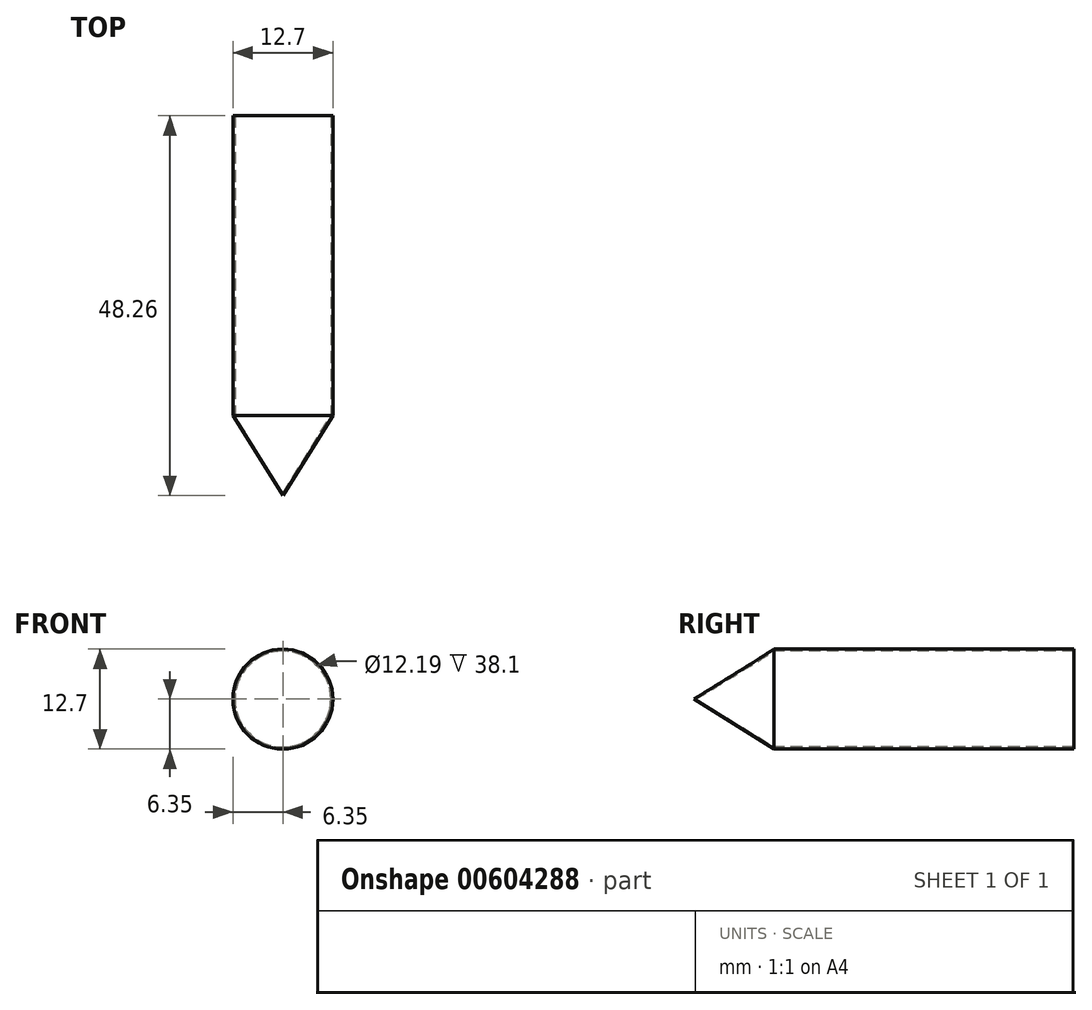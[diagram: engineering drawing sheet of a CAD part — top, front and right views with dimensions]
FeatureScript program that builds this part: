
annotation { "Feature Type Name" : "Feature", "Feature Type Description" : "" }
export const myFeature = defineFeature(function(context is Context, id is Id, definition is map)
    precondition{}
    {
        {
            var Q0;
            Q0=qCreatedBy(makeId("Right.planeOp"),FACE);
            var sketch = newSketch(context, id + "F0", { "sketchPlane" : qUnion([Q0])});
            skLineSegment(sketch, "E0.bottom", {"start": v(0, 0) * mm, "end": v(38.1, 0) * mm});
            skLineSegment(sketch, "E0.top", {"start": v(0, 6.35) * mm, "end": v(38.1, 6.35) * mm});
            skLineSegment(sketch, "E0.left", {"start": v(0, 0) * mm, "end": v(0, 6.35) * mm});
            skLineSegment(sketch, "E0.right", {"start": v(38.1, 0) * mm, "end": v(38.1, 6.35) * mm});
            skPoint(sketch, "E1.centerSnap0", {"position": v(0, 3.18) * mm});
            skLineSegment(sketch, "E2", {"start": v(0, 6.35) * mm, "end": v(-10.16, 0) * mm});
            skLineSegment(sketch, "E3", {"start": v(-10.16, 0) * mm, "end": v(0, 0) * mm});
            skLineSegment(sketch, "E4", {"start": v(0, 6.1) * mm, "end": v(38.1, 6.1) * mm});
            skLineSegment(sketch, "E5", {"start": v(0, 6.1) * mm, "end": v(-9.9, 0) * mm});
            skSolve(sketch);
        }
        {
            var Q0;
            {var subQ0=sQuery(id+"F0.wireOp",EDGE,"E2");Q0=makeQuery(id+"F0.imprint","IMPRINT",FACE,{"disambiguationData":[TD([[makeQuery(id+"F0.imprint","IMPRINT",EDGE,{"derivedFrom":subQ0}),1.0]])]});}
            var Q1;
            {var subQ0=sQuery(id+"F0.wireOp",EDGE,"E0.top");Q1=makeQuery(id+"F0.imprint","IMPRINT",FACE,{"disambiguationData":[TD([[makeQuery(id+"F0.imprint","IMPRINT",EDGE,{"derivedFrom":subQ0}),-1.0]])]});}
            var Q2;
            Q2=sQuery(id+"F0.wireOp",EDGE,"E0.bottom");
            revolve(context, id + "F1", {"entities" : qUnion([Q0, Q1]), "axis" : qUnion([Q2]), "revolveType" : RevolveType.FULL});
        }
    });
